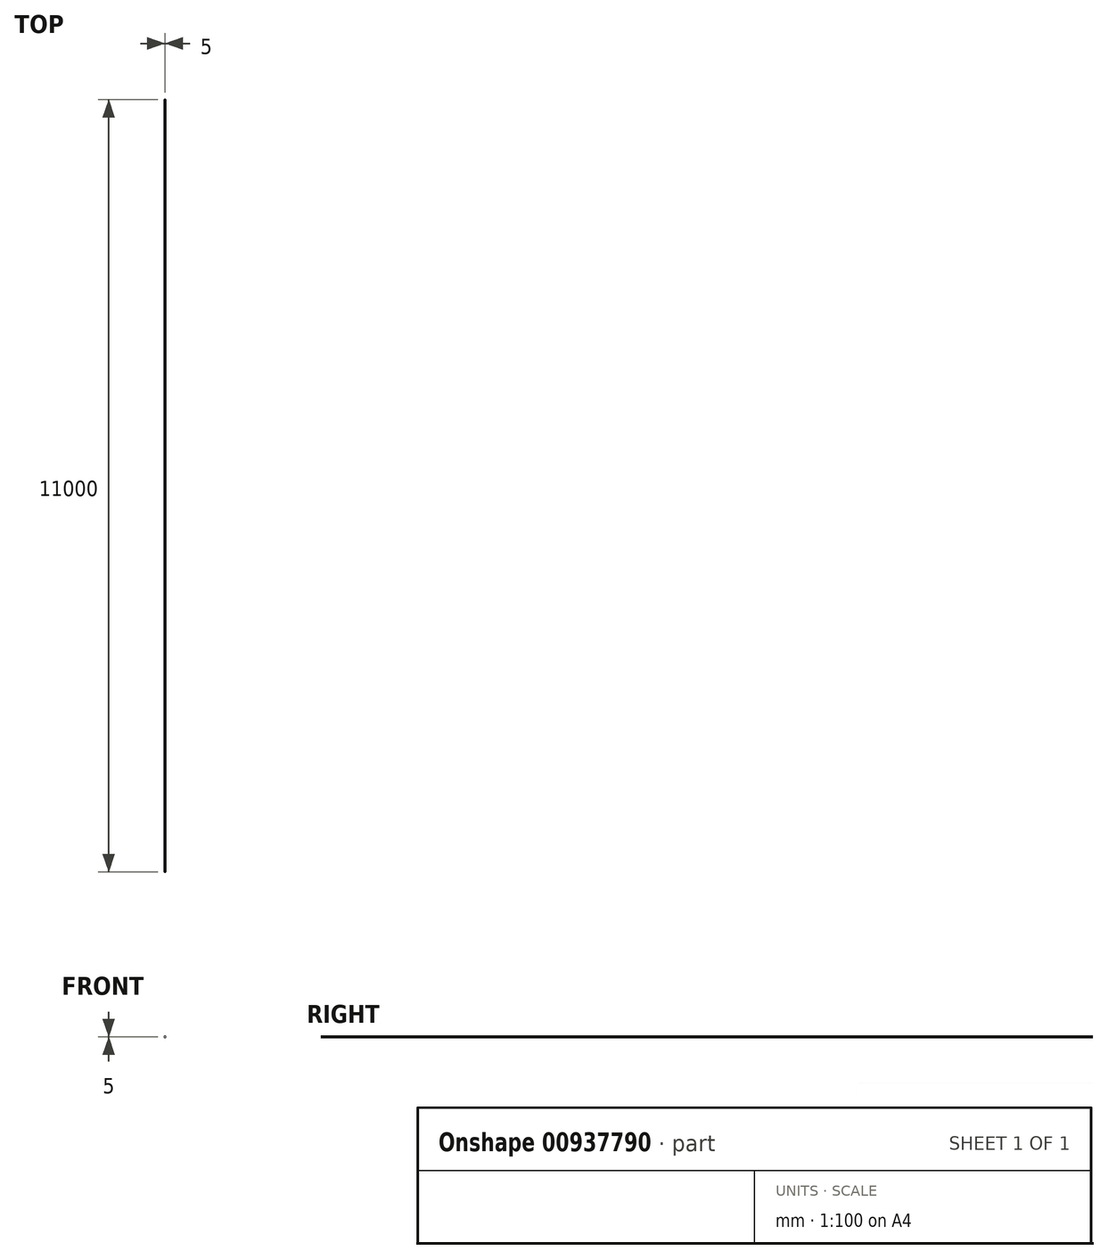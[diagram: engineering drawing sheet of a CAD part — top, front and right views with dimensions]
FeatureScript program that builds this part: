
annotation { "Feature Type Name" : "Feature", "Feature Type Description" : "" }
export const myFeature = defineFeature(function(context is Context, id is Id, definition is map)
    precondition{}
    {
        {
            var Q0;
            Q0=qCreatedBy(makeId("Front.planeOp"),FACE);
            var sketch = newSketch(context, id + "F0", { "sketchPlane" : qUnion([Q0])});
            skCircle(sketch, "E0", {"center": v(0, 0) * mm, "radius": 2.5 * mm});
            skSolve(sketch);
        }
        {
            var Q0;
            Q0=qSketchRegion(id+"F0",true);
            extrude(context, id + "F1", {"entities" : qUnion([Q0]), "depth" : 11000 * mm, "offsetDistance" : 25 * mm});
        }
    });
